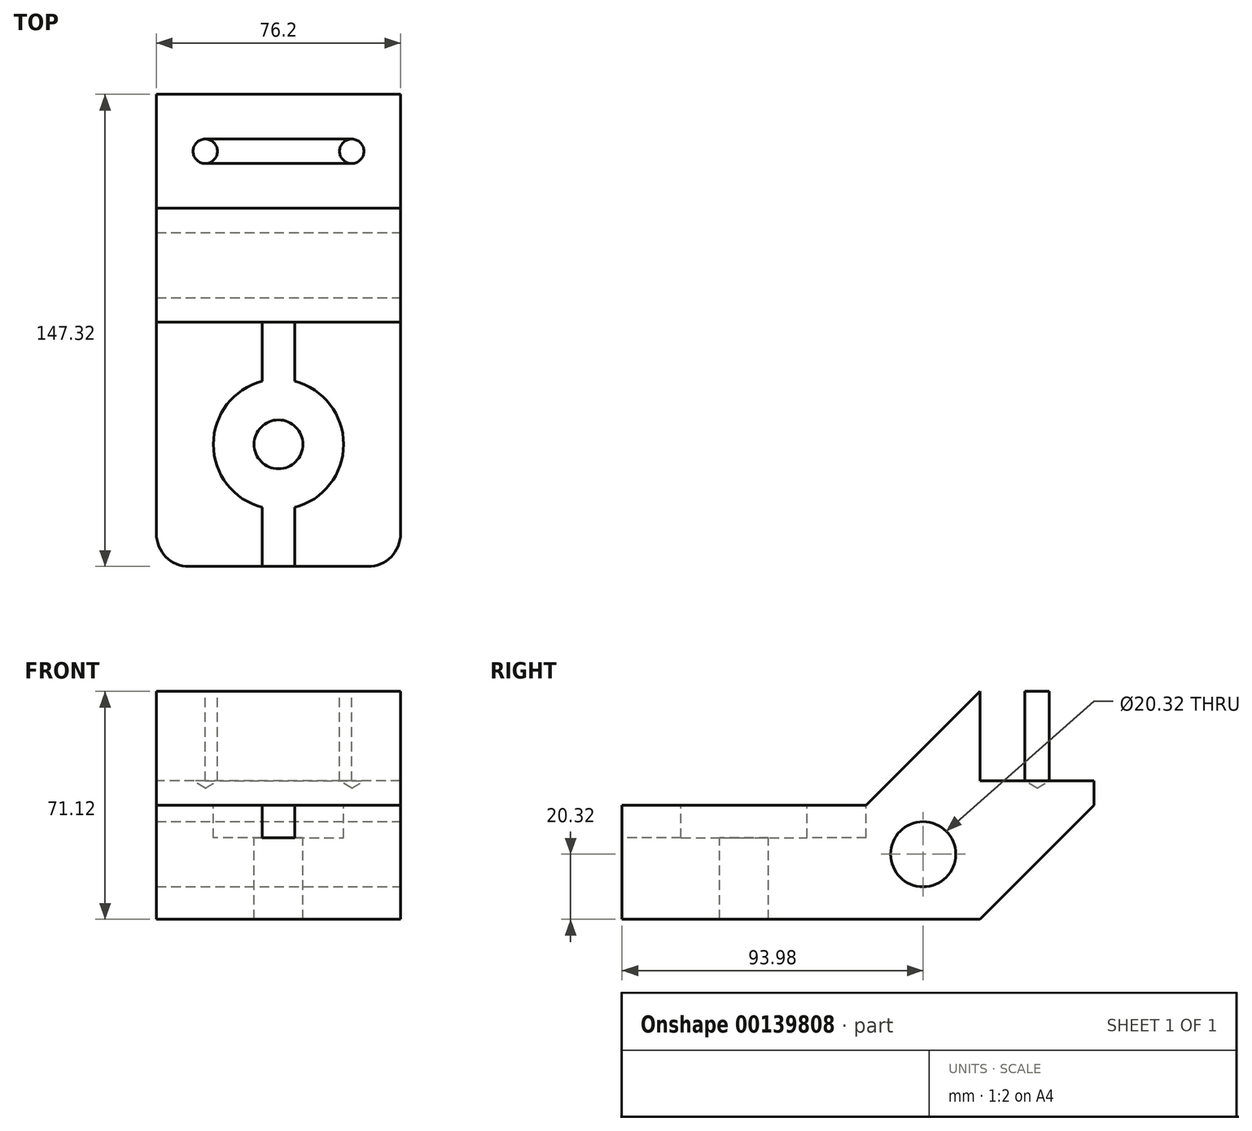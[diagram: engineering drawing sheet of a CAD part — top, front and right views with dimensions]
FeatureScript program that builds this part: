
annotation { "Feature Type Name" : "Feature", "Feature Type Description" : "" }
export const myFeature = defineFeature(function(context is Context, id is Id, definition is map)
    precondition{}
    {
        {
            var Q0;
            Q0=qCreatedBy(makeId("Right.planeOp"),FACE);
            var sketch = newSketch(context, id + "F0", { "sketchPlane" : qUnion([Q0])});
            skLineSegment(sketch, "E0", {"start": v(0, 0) * mm, "end": v(0, 35.56) * mm});
            skLineSegment(sketch, "E1", {"start": v(0, 35.56) * mm, "end": v(76.2, 35.56) * mm});
            skLineSegment(sketch, "E2", {"start": v(76.2, 35.56) * mm, "end": v(111.76, 71.12) * mm});
            skLineSegment(sketch, "E3", {"start": v(111.76, 71.12) * mm, "end": v(147.32, 71.12) * mm});
            skLineSegment(sketch, "E4", {"start": v(147.32, 71.12) * mm, "end": v(147.32, 35.56) * mm});
            skLineSegment(sketch, "E5", {"start": v(147.32, 35.56) * mm, "end": v(111.76, 0) * mm});
            skLineSegment(sketch, "E6", {"start": v(111.76, 0) * mm, "end": v(0, 0) * mm});
            skSolve(sketch);
        }
        {
            var Q0;
            Q0=makeQuery(id+"F0.imprint","IMPRINT",FACE,{"disambiguationData":[TD([[makeQuery(id+"F0.imprint","IMPRINT",EDGE,{"derivedFrom":sQuery(id+"F0.wireOp",EDGE,"E0")}),-1.0]])]});
            extrude(context, id + "F1", {"entities" : qUnion([Q0]), "depth" : 76.2 * mm});
        }
        {
            var Q0;
            Q0=makeQuery(id+"F1.opExtrude","SWEPT_FACE",FACE,{"disambiguationData":[OSD([sQuery(id+"F0.wireOp",EDGE,"E1")])]});
            var sketch = newSketch(context, id + "F2", { "sketchPlane" : qUnion([Q0])});
            skLineSegment(sketch, "E7.bottom", {"start": v(10.16, 0) * mm, "end": v(66.04, 0) * mm});
            skLineSegment(sketch, "E7.top", {"start": v(0, 76.2) * mm, "end": v(76.2, 76.2) * mm});
            skLineSegment(sketch, "E7.left", {"start": v(0, 10.16) * mm, "end": v(0, 76.2) * mm});
            skLineSegment(sketch, "E7.right", {"start": v(76.2, 10.16) * mm, "end": v(76.2, 76.2) * mm});
            skPoint(sketch, "E8.visualSharp", {"position": v(76.2, 0) * mm});
            skArc(sketch, "E8.filletArc", {"start": v(66.04, 0) * mm, "mid": v(73.22, 2.98) * mm, "end": v(76.2, 10.16) * mm});
            skPoint(sketch, "E9.visualSharp", {"position": v(0, 0) * mm});
            skArc(sketch, "E9.filletArc", {"start": v(0, 10.16) * mm, "mid": v(2.98, 2.98) * mm, "end": v(10.16, 0) * mm});
            skSolve(sketch);
        }
        {
            var Q0;
            {var subQ0=sQuery(id+"F2.wireOp",EDGE,"E9.filletArc");Q0=makeQuery(id+"F2.imprint","IMPRINT",FACE,{"disambiguationData":[TD([[makeQuery(id+"F2.imprint","IMPRINT",EDGE,{"derivedFrom":subQ0}),-1.0]])]});}
            var Q1;
            {var subQ0=sQuery(id+"F2.wireOp",EDGE,"E8.filletArc");Q1=makeQuery(id+"F2.imprint","IMPRINT",FACE,{"disambiguationData":[TD([[makeQuery(id+"F2.imprint","IMPRINT",EDGE,{"derivedFrom":subQ0}),-1.0]])]});}
            extrude(context, id + "F3", {"entities" : qUnion([Q0, Q1]), "operationType" : NewBodyOperationType.REMOVE, "endBound" : BoundingType.THROUGH_ALL, "oppositeDirection" : true, "depth" : 25.4 * mm});
        }
        {
            var Q0;
            Q0=makeQuery(id+"F1.opExtrude","CAP_FACE",FACE,{"disambiguationData":[OSD([sQuery(id+"F0.wireOp",EDGE,"E0"),sQuery(id+"F0.wireOp",EDGE,"E1"),sQuery(id+"F0.wireOp",EDGE,"E2"),sQuery(id+"F0.wireOp",EDGE,"E3"),sQuery(id+"F0.wireOp",EDGE,"E4"),sQuery(id+"F0.wireOp",EDGE,"E5"),sQuery(id+"F0.wireOp",EDGE,"E6")])],"isStart":false});
            var sketch = newSketch(context, id + "F4", { "sketchPlane" : qUnion([Q0])});
            skCircle(sketch, "E10", {"center": v(93.98, 20.32) * mm, "radius": 10.16 * mm});
            skSolve(sketch);
        }
        {
            var Q0;
            Q0=makeQuery(id+"F1.opExtrude","SWEPT_FACE",FACE,{"disambiguationData":[OSD([sQuery(id+"F0.wireOp",EDGE,"E3")])]});
            var sketch = newSketch(context, id + "F5", { "sketchPlane" : qUnion([Q0])});
            skLineSegment(sketch, "E11", {"start": v(15.24, 129.54) * mm, "end": v(60.96, 129.54) * mm, "construction": true});
            skArc(sketch, "E12.0.startCap", {"start": v(15.24, 125.73) * mm, "mid": v(11.43, 129.54) * mm, "end": v(15.24, 133.35) * mm});
            skArc(sketch, "E12.0.endCap", {"start": v(60.96, 133.35) * mm, "mid": v(64.77, 129.54) * mm, "end": v(60.96, 125.73) * mm});
            skLineSegment(sketch, "E12.0.left", {"start": v(15.24, 133.35) * mm, "end": v(60.96, 133.35) * mm});
            skLineSegment(sketch, "E12.0.right", {"start": v(15.24, 125.73) * mm, "end": v(60.96, 125.73) * mm});
            skSolve(sketch);
        }
        {
            var Q0;
            Q0=makeQuery(id+"F1.opExtrude","SWEPT_FACE",FACE,{"disambiguationData":[OSD([sQuery(id+"F0.wireOp",EDGE,"E1")])]});
            var sketch = newSketch(context, id + "F6", { "sketchPlane" : qUnion([Q0])});
            skCircle(sketch, "E13", {"center": v(38.1, 38.1) * mm, "radius": 7.62 * mm});
            skLineSegment(sketch, "E14.bottom", {"start": v(33.02, 76.2) * mm, "end": v(43.18, 76.2) * mm});
            skLineSegment(sketch, "E14.top", {"start": v(33.02, 0) * mm, "end": v(43.18, 0) * mm});
            skLineSegment(sketch, "E14.left", {"start": v(33.02, 76.2) * mm, "end": v(33.02, 0) * mm});
            skLineSegment(sketch, "E14.right", {"start": v(43.18, 76.2) * mm, "end": v(43.18, 0) * mm});
            skSolve(sketch);
        }
        {
            var Q0;
            Q0=sQuery(id+"F5.wireOp",VERTEX,"E11.start");
            var Q1;
            Q1=sQuery(id+"F5.wireOp",VERTEX,"E11.end");
            var Q2;
            Q2=makeQuery(id+"F1.opExtrude","SWEPT_BODY",BODY,{"disambiguationData":[OSD([sQuery(id+"F0.wireOp",EDGE,"E0"),sQuery(id+"F0.wireOp",EDGE,"E1"),sQuery(id+"F0.wireOp",EDGE,"E2"),sQuery(id+"F0.wireOp",EDGE,"E3"),sQuery(id+"F0.wireOp",EDGE,"E4"),sQuery(id+"F0.wireOp",EDGE,"E5"),sQuery(id+"F0.wireOp",EDGE,"E6")])]});
            hole(context, id + "F7", {"style" : HoleStyle.SIMPLE, "endStyle" : HoleEndStyle.BLIND, "holeDiameter" : 7.62 * mm, "holeDepth" : 27.94 * mm, "startFromSketch" : true, "locations" : qUnion([Q0, Q1]), "scope" : qUnion([Q2])});
        }
        {
            var Q0;
            Q0=makeQuery(id+"F5.imprint","IMPRINT",FACE,{"disambiguationData":[TD([[makeQuery(id+"F5.imprint","IMPRINT",EDGE,{"derivedFrom":sQuery(id+"F5.wireOp",EDGE,"E12.0.startCap")}),-1.0]])]});
            extrude(context, id + "F8", {"entities" : qUnion([Q0]), "operationType" : NewBodyOperationType.REMOVE, "oppositeDirection" : true, "depth" : 27.94 * mm});
        }
        {
            var Q0;
            Q0=sQuery(id+"F6.wireOp",VERTEX,"E13.center");
            var Q1;
            Q1=makeQuery(id+"F1.opExtrude","SWEPT_BODY",BODY,{"disambiguationData":[OSD([sQuery(id+"F0.wireOp",EDGE,"E0"),sQuery(id+"F0.wireOp",EDGE,"E1"),sQuery(id+"F0.wireOp",EDGE,"E2"),sQuery(id+"F0.wireOp",EDGE,"E3"),sQuery(id+"F0.wireOp",EDGE,"E4"),sQuery(id+"F0.wireOp",EDGE,"E5"),sQuery(id+"F0.wireOp",EDGE,"E6")])]});
            hole(context, id + "F9", {"style" : HoleStyle.C_BORE, "endStyle" : HoleEndStyle.THROUGH, "holeDiameter" : 15.24 * mm, "cBoreDiameter" : 40.64 * mm, "cBoreDepth" : 10.16 * mm, "startFromSketch" : true, "locations" : qUnion([Q0]), "scope" : qUnion([Q1]), "isTappedThrough" : true});
        }
        {
            var Q0;
            {var subQ5=sQuery(id+"F6.wireOp",EDGE,"E14.top");Q0=makeQuery(id+"F6.imprint","IMPRINT",FACE,{"disambiguationData":[TD([[makeQuery(id+"F6.imprint","IMPRINT",EDGE,{"derivedFrom":subQ5}),-1.0]])]});}
            var Q1;
            {var subQ5=sQuery(id+"F6.wireOp",EDGE,"E14.bottom");Q1=makeQuery(id+"F6.imprint","IMPRINT",FACE,{"disambiguationData":[TD([[makeQuery(id+"F6.imprint","IMPRINT",EDGE,{"derivedFrom":subQ5}),1.0]])]});}
            extrude(context, id + "F10", {"entities" : qUnion([Q0, Q1]), "operationType" : NewBodyOperationType.REMOVE, "oppositeDirection" : true, "depth" : 10.16 * mm});
        }
        {
            var Q0;
            Q0=makeQuery(id+"F4.imprint","IMPRINT",FACE,{"disambiguationData":[TD([[makeQuery(id+"F4.imprint","IMPRINT",EDGE,{"derivedFrom":sQuery(id+"F4.wireOp",EDGE,"E10")}),1.0]])]});
            extrude(context, id + "F11", {"entities" : qUnion([Q0]), "operationType" : NewBodyOperationType.REMOVE, "endBound" : BoundingType.THROUGH_ALL, "oppositeDirection" : true, "depth" : 25.4 * mm});
        }
    });
